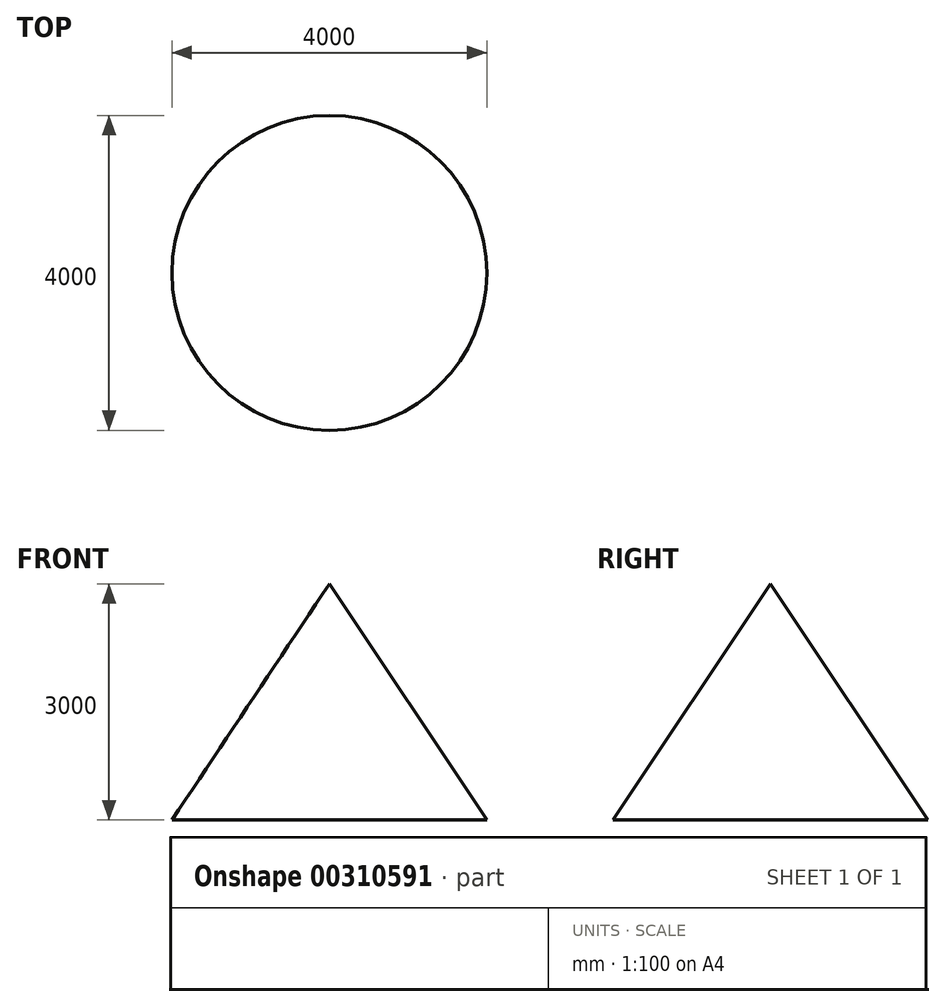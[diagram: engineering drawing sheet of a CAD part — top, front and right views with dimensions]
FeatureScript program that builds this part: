
annotation { "Feature Type Name" : "Feature", "Feature Type Description" : "" }
export const myFeature = defineFeature(function(context is Context, id is Id, definition is map)
    precondition{}
    {
        {
            var Q0;
            Q0=qCreatedBy(makeId("Front.planeOp"),FACE);
            var sketch = newSketch(context, id + "F0", { "sketchPlane" : qUnion([Q0])});
            skLineSegment(sketch, "E0", {"start": v(0, 0) * mm, "end": v(0, 3000) * mm});
            skLineSegment(sketch, "E1", {"start": v(0, 0) * mm, "end": v(2000, 0) * mm});
            skLineSegment(sketch, "E2", {"start": v(2000, 0) * mm, "end": v(0, 3000) * mm});
            skSolve(sketch);
        }
        {
            var Q0;
            Q0 = qSketchRegion(id + "F0", true);
            var Q1;
            Q1=sQuery(id+"F0.wireOp",EDGE,"E0");
            revolve(context, id + "F1", {"entities" : qUnion([Q0]), "axis" : qUnion([Q1]), "revolveType" : RevolveType.FULL});
        }
    });
